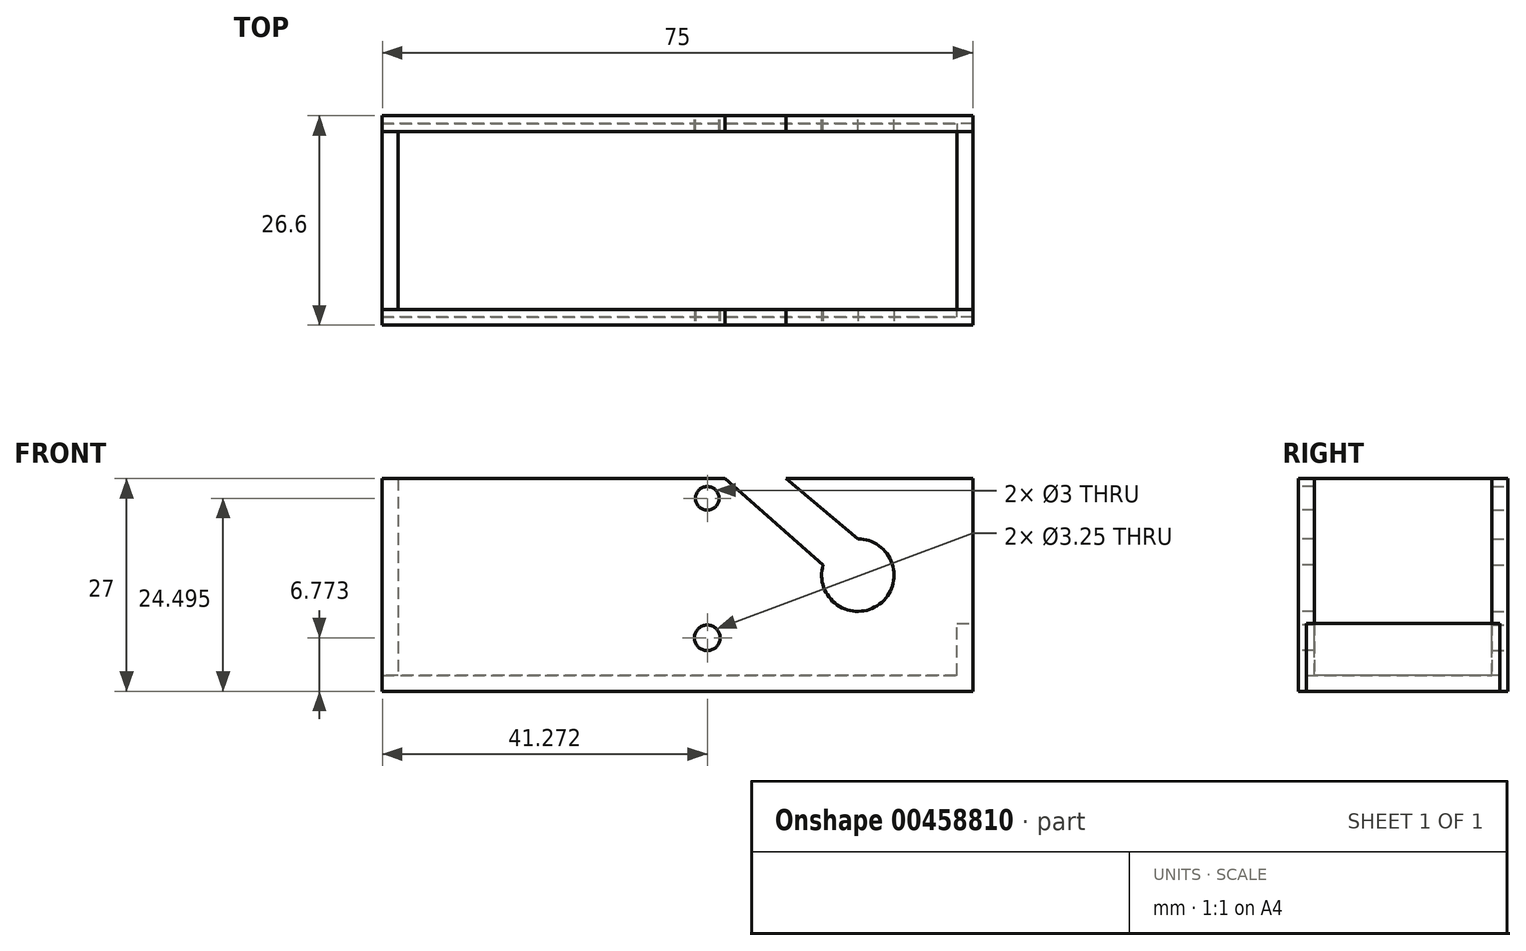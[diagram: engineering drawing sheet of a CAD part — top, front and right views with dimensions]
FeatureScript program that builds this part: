
annotation { "Feature Type Name" : "Feature", "Feature Type Description" : "" }
export const myFeature = defineFeature(function(context is Context, id is Id, definition is map)
    precondition{}
    {
        {
            var Q0;
            Q0=qCreatedBy(makeId("Front.planeOp"),FACE);
            var sketch = newSketch(context, id + "F0", { "sketchPlane" : qUnion([Q0])});
            skCircle(sketch, "E0", {"center": v(13.76, -2.57) * mm, "radius": 1.62 * mm});
            skCircle(sketch, "E1.MirrorC", {"center": v(13.76, 15.16) * mm, "radius": 1.5 * mm});
            skLineSegment(sketch, "E2.0", {"start": v(47.49, 6.3) * mm, "end": v(47.49, 17.66) * mm});
            skLineSegment(sketch, "E2.3", {"start": v(47.49, 17.66) * mm, "end": v(23.76, 17.66) * mm});
            skLineSegment(sketch, "E2.4", {"start": v(47.49, -9.34) * mm, "end": v(5.93, -9.34) * mm});
            skLineSegment(sketch, "E2.5", {"start": v(47.49, 6.3) * mm, "end": v(47.49, -9.34) * mm});
            skLineSegment(sketch, "E3", {"start": v(1.2, -7.34) * mm, "end": v(45.49, -7.34) * mm});
            skPoint(sketch, "E4", {"position": v(32.89, 5.4) * mm});
            skLineSegment(sketch, "E5.trimOffspring", {"start": v(15.99, 17.66) * mm, "end": v(-5.28, 17.66) * mm});
            skLineSegment(sketch, "E6", {"start": v(5.93, -9.34) * mm, "end": v(-27.51, -9.34) * mm});
            skLineSegment(sketch, "E7", {"start": v(-27.51, -7.34) * mm, "end": v(-27.51, -9.34) * mm});
            skLineSegment(sketch, "E8", {"start": v(1.2, -7.34) * mm, "end": v(-27.51, -7.34) * mm});
            skLineSegment(sketch, "E9", {"start": v(-5.28, 17.66) * mm, "end": v(-27.51, 17.66) * mm});
            skLineSegment(sketch, "E10", {"start": v(-27.51, 17.66) * mm, "end": v(-27.51, -7.34) * mm});
            skLineSegment(sketch, "E11", {"start": v(-25.51, -7.34) * mm, "end": v(-25.51, 17.66) * mm});
            skLineSegment(sketch, "E12", {"start": v(47.49, -0.72) * mm, "end": v(45.49, -0.72) * mm});
            skLineSegment(sketch, "E13", {"start": v(45.49, -0.72) * mm, "end": v(45.49, -9.34) * mm});
            skArc(sketch, "E14", {"start": v(28.48, 6.7) * mm, "mid": v(35.65, 1.72) * mm, "end": v(32.89, 10) * mm});
            skLineSegment(sketch, "E15", {"start": v(32.89, 10) * mm, "end": v(23.76, 17.66) * mm});
            skLineSegment(sketch, "E16", {"start": v(15.99, 17.66) * mm, "end": v(28.48, 6.7) * mm});
            skPoint(sketch, "E17", {"position": v(37.49, 5.4) * mm});
            skPoint(sketch, "E18", {"position": v(12.14, -2.57) * mm});
            skPoint(sketch, "E19", {"position": v(13.76, -0.94) * mm});
            skPoint(sketch, "E20", {"position": v(13.76, 13.66) * mm});
            skSolve(sketch);
        }
        {
            var Q0;
            Q0 = qSketchRegion(id + "F0", true);
            extrude(context, id + "F1", {"entities" : qUnion([Q0]), "depth" : 2 * mm, "offsetDistance" : 25.4 * mm});
        }
        {
            var Q0;
            {var subQ0=sQuery(id+"F0.wireOp",EDGE,"E2.4");Q0=makeQuery(id+"F0.imprint","IMPRINT",FACE,{"disambiguationData":[TD([[makeQuery(id+"F0.imprint","IMPRINT",EDGE,{"derivedFrom":subQ0}),-1.0]])]});}
            var Q1;
            {var subQ5=sQuery(id+"F0.wireOp",EDGE,"E3");Q1=makeQuery(id+"F0.imprint","IMPRINT",FACE,{"disambiguationData":[TD([[makeQuery(id+"F0.imprint","IMPRINT",EDGE,{"derivedFrom":subQ5}),-1.0]])]});}
            extrude(context, id + "F2", {"entities" : qUnion([Q0, Q1]), "depth" : 25.6 * mm, "offsetDistance" : 25.4 * mm});
        }
        {
            var Q0;
            {var subQ0=sQuery(id+"F0.wireOp",EDGE,"E10");Q0=makeQuery(id+"F0.imprint","IMPRINT",FACE,{"disambiguationData":[TD([[makeQuery(id+"F0.imprint","IMPRINT",EDGE,{"derivedFrom":subQ0}),1.0]])]});}
            extrude(context, id + "F3", {"entities" : qUnion([Q0]), "operationType" : NewBodyOperationType.ADD, "depth" : 24.6 * mm, "offsetDistance" : 25.4 * mm});
        }
        {
            var Q0;
            Q0=qCreatedBy(makeId("Front.planeOp"),FACE);
            cPlane(context, id + "F4", {"entities" : qUnion([Q0]), "cplaneType" : CPlaneType.OFFSET, "offset" : 13.3 * mm, "width" : 152.4 * mm, "height" : 152.4 * mm});
        }
        {
            var Q0;
            Q0=makeQuery(id+"F1.opExtrude","SWEPT_BODY",BODY,{"disambiguationData":[OSD([sQuery(id+"F0.wireOp",EDGE,"E0"),sQuery(id+"F0.wireOp",EDGE,"E1.MirrorC"),sQuery(id+"F0.wireOp",EDGE,"E2.0"),sQuery(id+"F0.wireOp",EDGE,"E2.3"),sQuery(id+"F0.wireOp",EDGE,"E2.4"),sQuery(id+"F0.wireOp",EDGE,"E2.5"),sQuery(id+"F0.wireOp",EDGE,"E5.trimOffspring"),sQuery(id+"F0.wireOp",EDGE,"E6"),sQuery(id+"F0.wireOp",EDGE,"E7"),sQuery(id+"F0.wireOp",EDGE,"E9"),sQuery(id+"F0.wireOp",EDGE,"E10"),sQuery(id+"F0.wireOp",EDGE,"E14"),sQuery(id+"F0.wireOp",EDGE,"E15"),sQuery(id+"F0.wireOp",EDGE,"E16")])]});
            var Q1;
            Q1=qCreatedBy(id+"F4.planeOp",FACE);
            mirror(context, id + "F5", {"entities" : qUnion([Q0]), "mirrorPlane" : qUnion([Q1])});
        }
    });
